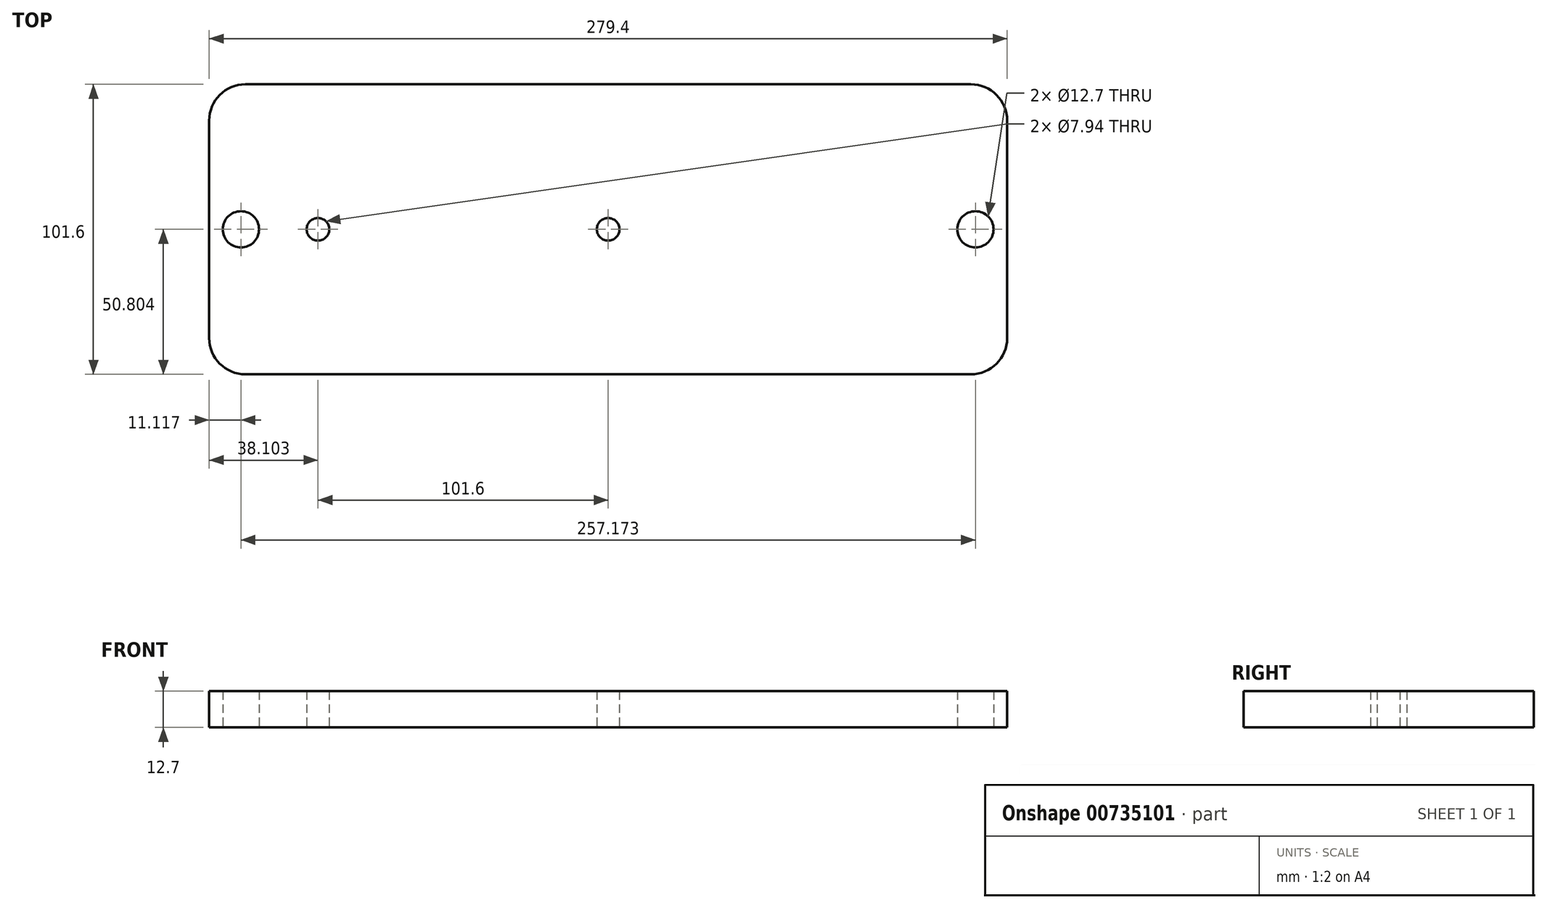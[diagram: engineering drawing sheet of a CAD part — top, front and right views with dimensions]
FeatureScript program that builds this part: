
annotation { "Feature Type Name" : "Feature", "Feature Type Description" : "" }
export const myFeature = defineFeature(function(context is Context, id is Id, definition is map)
    precondition{}
    {
        {
            var Q0;
            Q0=qCreatedBy(makeId("Top.planeOp"),FACE);
            var sketch = newSketch(context, id + "F0", { "sketchPlane" : qUnion([Q0])});
            skLineSegment(sketch, "E0", {"start": v(-67.23, 59.64) * mm, "end": v(186.77, 59.64) * mm});
            skLineSegment(sketch, "E1", {"start": v(199.47, 46.94) * mm, "end": v(199.47, -29.26) * mm});
            skLineSegment(sketch, "E2", {"start": v(186.77, -41.96) * mm, "end": v(-67.23, -41.96) * mm});
            skLineSegment(sketch, "E3", {"start": v(-79.93, -29.26) * mm, "end": v(-79.93, 46.94) * mm});
            skPoint(sketch, "E4.visualSharp", {"position": v(-79.93, 59.64) * mm});
            skArc(sketch, "E4.filletArc", {"start": v(-67.23, 59.64) * mm, "mid": v(-76.2, 55.92) * mm, "end": v(-79.93, 46.94) * mm});
            skPoint(sketch, "E5.visualSharp", {"position": v(199.47, 59.64) * mm});
            skArc(sketch, "E5.filletArc", {"start": v(199.47, 46.94) * mm, "mid": v(195.75, 55.92) * mm, "end": v(186.77, 59.64) * mm});
            skPoint(sketch, "E6.visualSharp", {"position": v(199.47, -41.96) * mm});
            skArc(sketch, "E6.filletArc", {"start": v(186.77, -41.96) * mm, "mid": v(195.75, -38.24) * mm, "end": v(199.47, -29.26) * mm});
            skPoint(sketch, "E7.visualSharp", {"position": v(-79.93, -41.96) * mm});
            skArc(sketch, "E7.filletArc", {"start": v(-79.93, -29.26) * mm, "mid": v(-76.2, -38.24) * mm, "end": v(-67.23, -41.96) * mm});
            skLineSegment(sketch, "E8", {"start": v(-85.16, 8.84) * mm, "end": v(204.7, 8.84) * mm, "construction": true});
            skPoint(sketch, "E8.startSnap0", {"position": v(-79.93, 8.84) * mm});
            skCircle(sketch, "E9", {"center": v(-68.81, 8.84) * mm, "radius": 6.35 * mm});
            skCircle(sketch, "E10", {"center": v(-41.83, 8.84) * mm, "radius": 3.97 * mm});
            skCircle(sketch, "E11", {"center": v(59.77, 8.84) * mm, "radius": 3.97 * mm});
            skCircle(sketch, "E12", {"center": v(188.36, 8.84) * mm, "radius": 6.35 * mm});
            skSolve(sketch);
        }
        {
            var Q0;
            Q0=qSketchRegion(id+"F0",true);
            extrude(context, id + "F1", {"entities" : qUnion([Q0]), "endBound" : BoundingType.SYMMETRIC, "depth" : 12.7 * mm, "offsetDistance" : 25.4 * mm});
        }
    });
